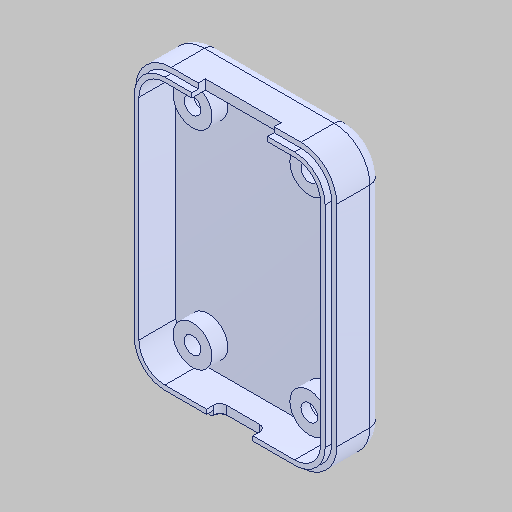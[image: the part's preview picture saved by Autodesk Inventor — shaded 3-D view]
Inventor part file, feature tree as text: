
AUTODESK INVENTOR PART (.ipt)
format: ipt  version: 2023.5 (Build 275446000, 446)  size: 241,152 bytes
history: native  units: in
note: dims shown in document units (in); Inventor stores cm internally (conversion verified against a paired STEP export)
features: fillet x1
ambient origin geometry x8: Origin, YZ Plane, XZ Plane, XY Plane, X Axis, Y Axis, Z Axis, Center Point
bodies: Solid1 (feature_tree)
feature tree (1):
  fillet  "Fillet5"  [1 undecoded]
note: 1 required parameter value undecoded (feature->parameter linkage not recoverable at this tier; creation-order binding heuristic only, values carry confidence <= 0.55)
